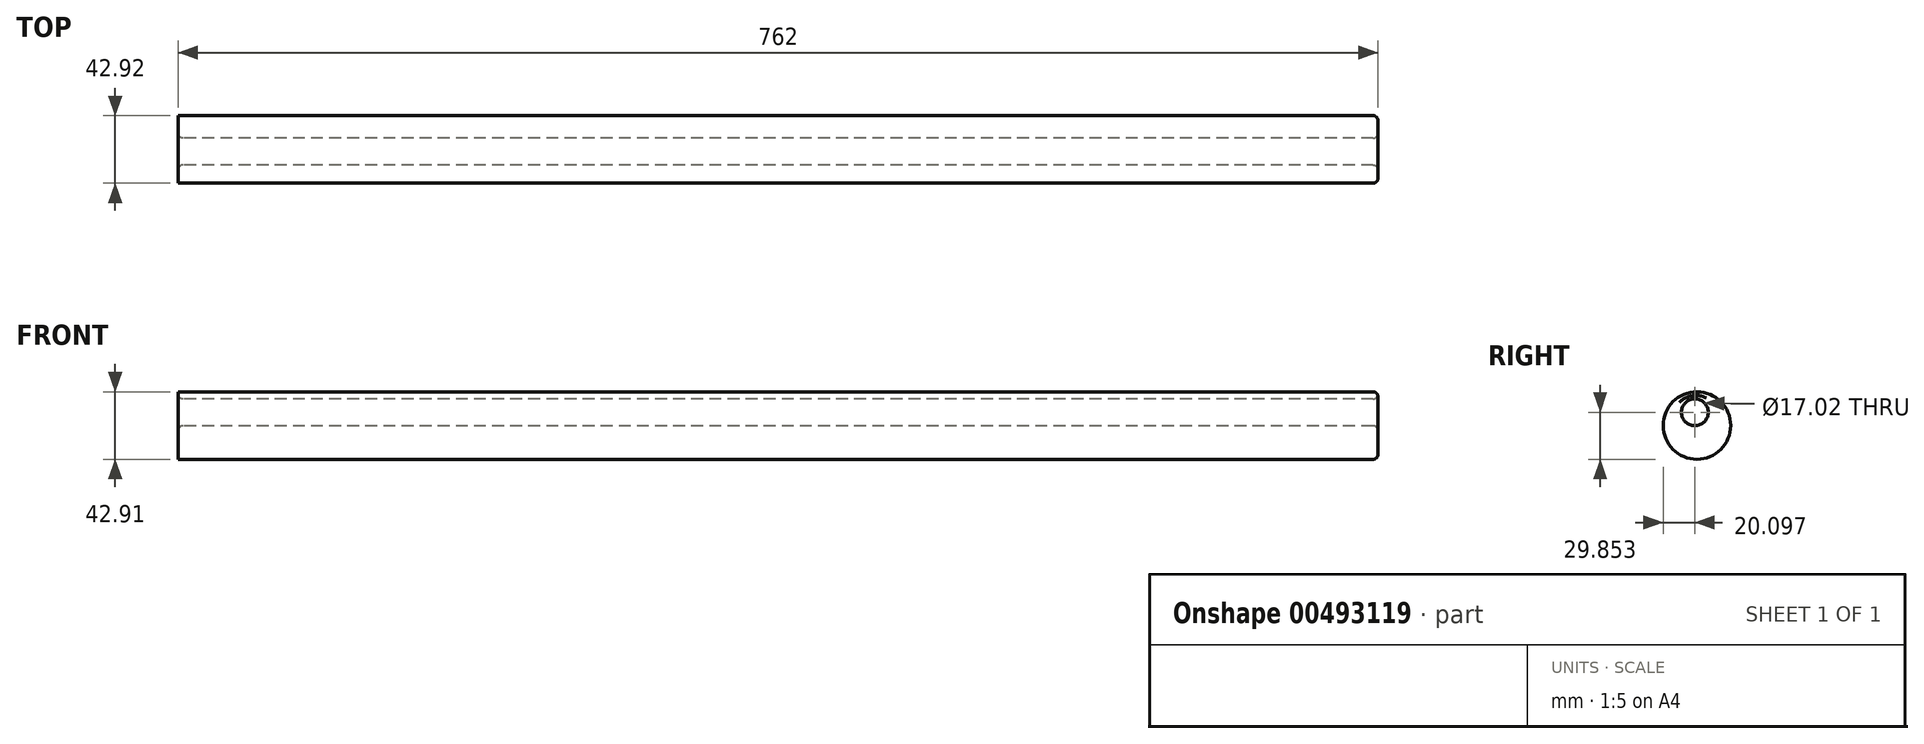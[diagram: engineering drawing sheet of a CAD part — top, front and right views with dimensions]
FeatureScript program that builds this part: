
annotation { "Feature Type Name" : "Feature", "Feature Type Description" : "" }
export const myFeature = defineFeature(function(context is Context, id is Id, definition is map)
    precondition{}
    {
        {
            var Q0;
            Q0=qCreatedBy(makeId("Right.planeOp"),FACE);
            var sketch = newSketch(context, id + "F0", { "sketchPlane" : qUnion([Q0])});
            skCircle(sketch, "E0", {"center": v(-29.8, 29.8) * mm, "radius": 8.51 * mm});
            skCircle(sketch, "E1", {"center": v(-28.44, 21.4) * mm, "radius": 21.46 * mm});
            skSolve(sketch);
        }
        {
            var Q0;
            Q0 = qSketchRegion(id + "F0", true);
            extrude(context, id + "F1", {"entities" : qUnion([Q0]), "depth" : 762 * mm});
        }
        {
            var Q0;
            Q0=makeQuery(id+"F1.opExtrude","CAP_EDGE",EDGE,{"disambiguationData":[OSD([sQuery(id+"F0.wireOp",EDGE,"E1")])],"isStart":false});
            var Q1;
            Q1=makeQuery(id+"F1.opExtrude","CAP_EDGE",EDGE,{"disambiguationData":[OSD([sQuery(id+"F0.wireOp",EDGE,"E0")])],"isStart":false});
            var Q2;
            Q2=makeQuery(id+"F1.opExtrude","SWEPT_FACE",FACE,{"disambiguationData":[OSD([sQuery(id+"F0.wireOp",EDGE,"E0")])]});
            fillet(context, id + "F2", {"entities" : qUnion([Q0, Q1, Q2]), "radius" : 3.07 * mm, "tangentPropagation" : true, "allowEdgeOverflow" : false});
        }
    });
